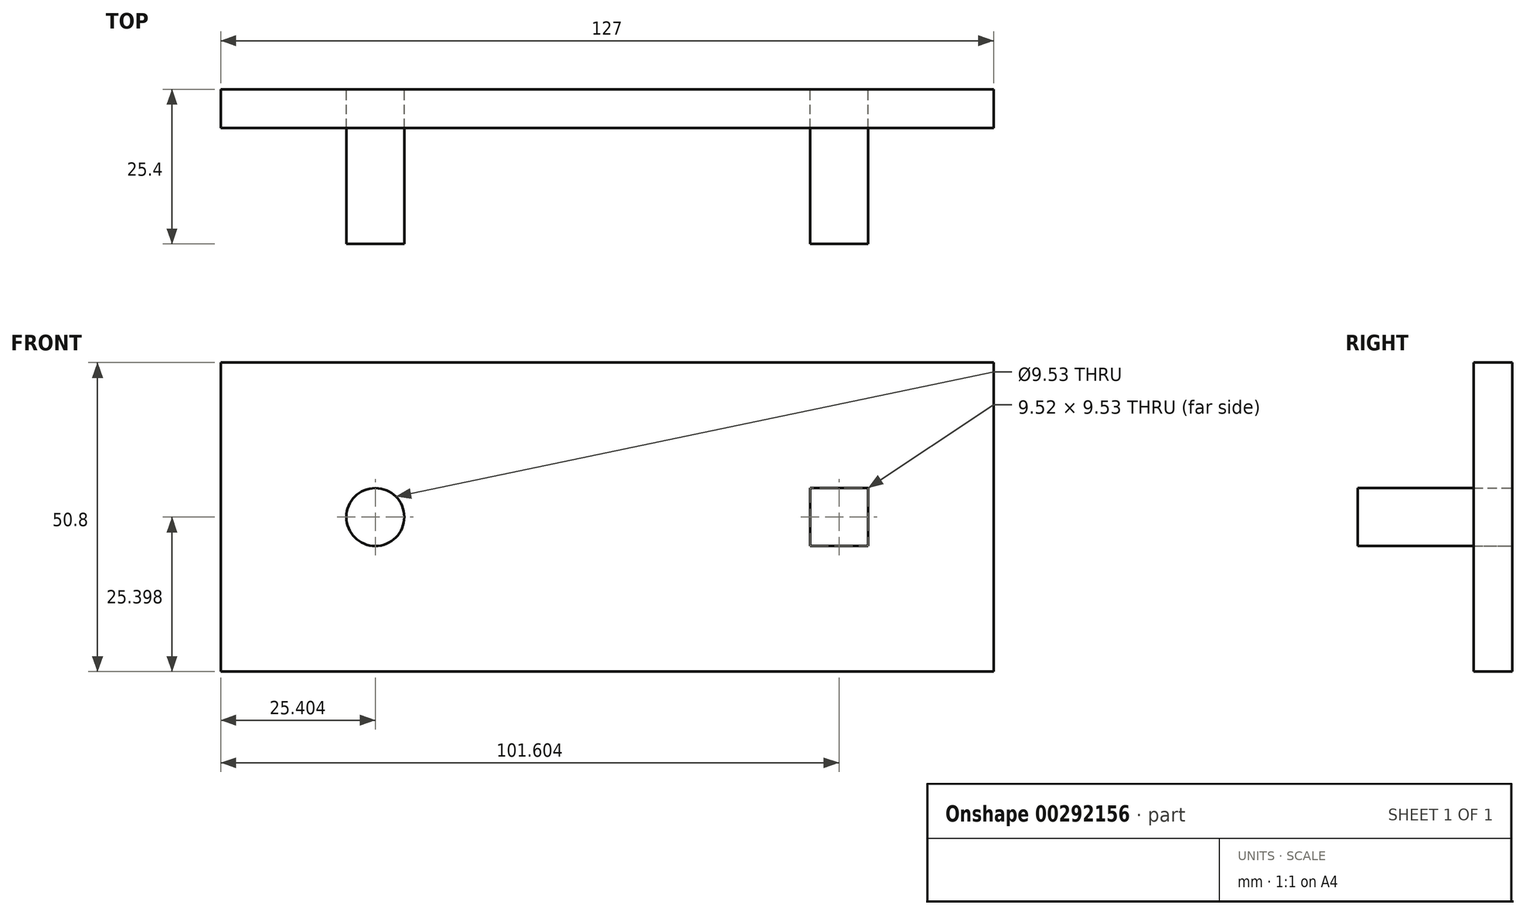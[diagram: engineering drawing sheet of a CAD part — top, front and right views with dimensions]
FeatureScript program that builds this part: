
annotation { "Feature Type Name" : "Feature", "Feature Type Description" : "" }
export const myFeature = defineFeature(function(context is Context, id is Id, definition is map)
    precondition{}
    {
        {
            var Q0;
            Q0=qCreatedBy(makeId("Front.planeOp"),FACE);
            var sketch = newSketch(context, id + "F0", { "sketchPlane" : qUnion([Q0])});
            skLineSegment(sketch, "E0.bottom", {"start": v(-54.05, 20.64) * mm, "end": v(72.95, 20.64) * mm});
            skLineSegment(sketch, "E0.top", {"start": v(-54.05, -30.16) * mm, "end": v(72.95, -30.16) * mm});
            skLineSegment(sketch, "E0.left", {"start": v(-54.05, 20.64) * mm, "end": v(-54.05, -30.16) * mm});
            skLineSegment(sketch, "E0.right", {"start": v(72.95, 20.64) * mm, "end": v(72.95, -30.16) * mm});
            skPoint(sketch, "E1.oppositeSnap0", {"position": v(-54.05, -4.76) * mm});
            skLineSegment(sketch, "E1.bottom", {"start": v(-54.05, -4.76) * mm, "end": v(-28.65, -4.76) * mm});
            skLineSegment(sketch, "E1.left", {"start": v(-54.05, -4.76) * mm, "end": v(-54.05, -4.76) * mm});
            skLineSegment(sketch, "E1.right", {"start": v(-28.65, -4.76) * mm, "end": v(-28.65, -4.76) * mm});
            skLineSegment(sketch, "E2", {"start": v(72.95, -4.76) * mm, "end": v(47.55, -4.76) * mm});
            skCircle(sketch, "E3", {"center": v(-28.65, -4.76) * mm, "radius": 4.76 * mm});
            skPoint(sketch, "E4.middle", {"position": v(47.55, -4.76) * mm});
            skLineSegment(sketch, "E5.bottom", {"start": v(42.8, 0) * mm, "end": v(52.32, 0) * mm});
            skLineSegment(sketch, "E5.top", {"start": v(42.8, -9.53) * mm, "end": v(52.32, -9.53) * mm});
            skLineSegment(sketch, "E5.left", {"start": v(42.8, 0) * mm, "end": v(42.8, -9.53) * mm});
            skLineSegment(sketch, "E5.right", {"start": v(52.32, 0) * mm, "end": v(52.32, -9.53) * mm});
            skSolve(sketch);
        }
        {
            var Q0;
            Q0=makeQuery(id+"F0.imprint","IMPRINT",FACE,{"disambiguationData":[TD([[makeQuery(id+"F0.imprint","IMPRINT",EDGE,{"derivedFrom":sQuery(id+"F0.wireOp",EDGE,"E3")}),1.0]])]});
            var Q1;
            {var subQ1=sQuery(id+"F0.wireOp",EDGE,"E5.bottom");Q1=makeQuery(id+"F0.imprint","IMPRINT",FACE,{"disambiguationData":[TD([[makeQuery(id+"F0.imprint","IMPRINT",EDGE,{"derivedFrom":subQ1}),-1.0]])]});}
            extrude(context, id + "F1", {"entities" : qUnion([Q0, Q1]), "depth" : 25.4 * mm});
        }
        {
            var Q0;
            {var subQ5=sQuery(id+"F0.wireOp",EDGE,"E0.bottom");Q0=makeQuery(id+"F0.imprint","IMPRINT",FACE,{"disambiguationData":[TD([[makeQuery(id+"F0.imprint","IMPRINT",EDGE,{"derivedFrom":subQ5}),-1.0]])]});}
            extrude(context, id + "F2", {"entities" : qUnion([Q0]), "depth" : 6.35 * mm});
        }
    });
